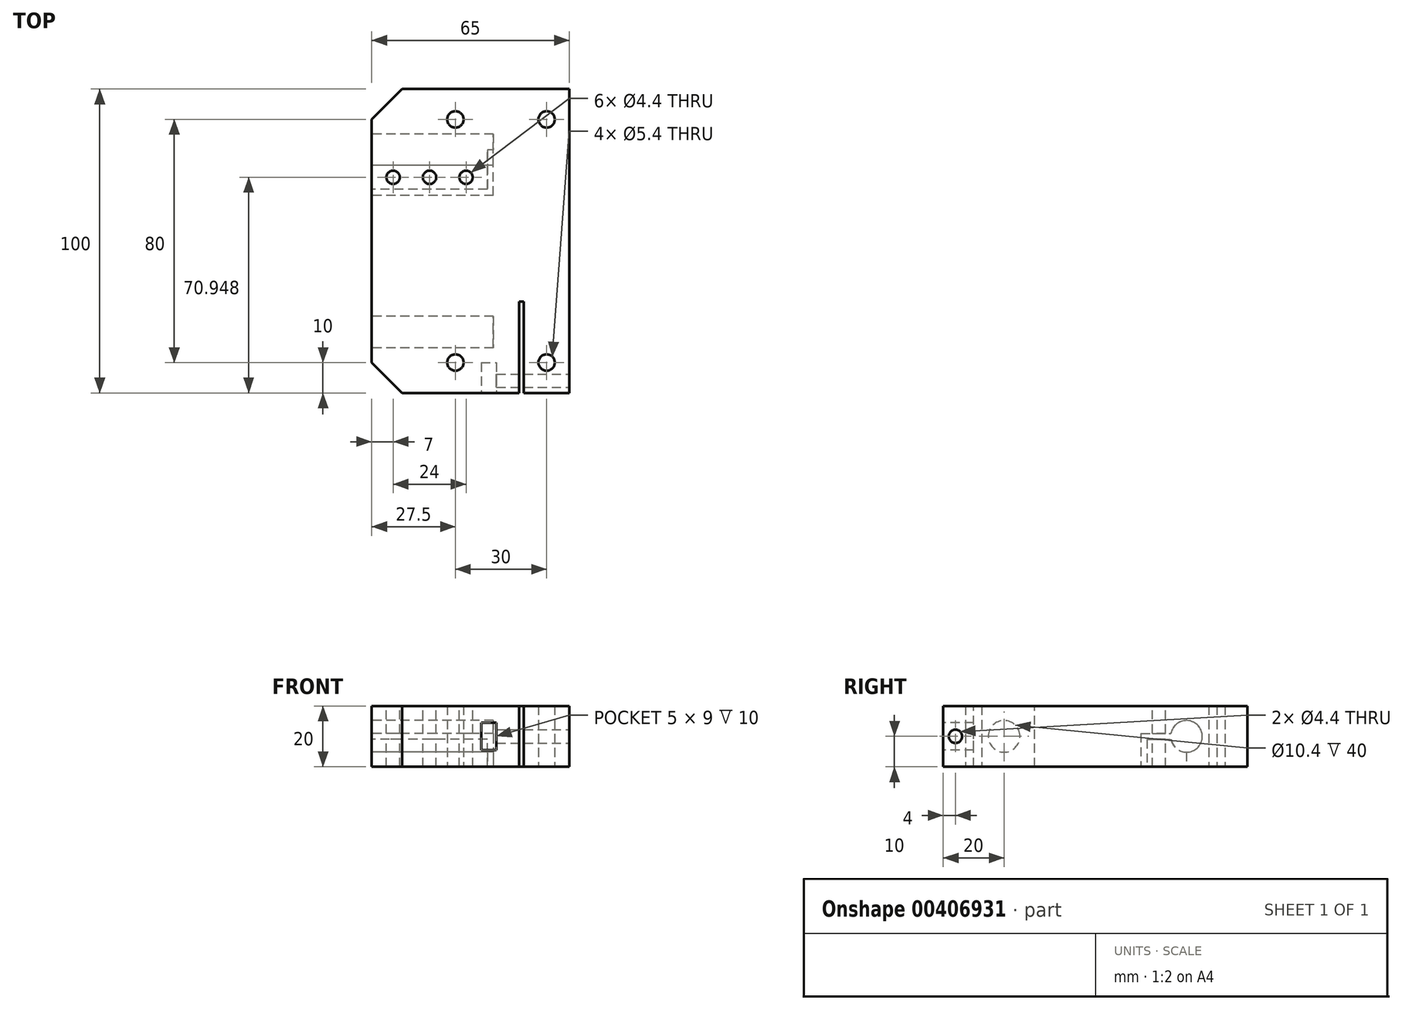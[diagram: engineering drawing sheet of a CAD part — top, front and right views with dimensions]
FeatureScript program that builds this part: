
annotation { "Feature Type Name" : "Feature", "Feature Type Description" : "" }
export const myFeature = defineFeature(function(context is Context, id is Id, definition is map)
    precondition{}
    {
        {
            var Q0;
            Q0=qCreatedBy(makeId("Top.planeOp"),FACE);
            var sketch = newSketch(context, id + "F0", { "sketchPlane" : qUnion([Q0])});
            skLineSegment(sketch, "E0", {"start": v(-15, 15.7) * mm, "end": v(-15, -27.72) * mm, "construction": true});
            skCircle(sketch, "E1", {"center": v(-15, 40) * mm, "radius": 2.7 * mm});
            skCircle(sketch, "E2", {"center": v(-15, -40) * mm, "radius": 2.7 * mm});
            skCircle(sketch, "E3.MirrorC", {"center": v(15, 40) * mm, "radius": 2.7 * mm});
            skCircle(sketch, "E4.MirrorC", {"center": v(15, -40) * mm, "radius": 2.7 * mm});
            skLineSegment(sketch, "E5.bottom", {"start": v(22.5, -50) * mm, "end": v(-22.5, -50) * mm});
            skLineSegment(sketch, "E5.top", {"start": v(22.5, 50) * mm, "end": v(-22.5, 50) * mm});
            skLineSegment(sketch, "E5.left", {"start": v(22.5, -50) * mm, "end": v(22.5, 50) * mm});
            skLineSegment(sketch, "E5.right", {"start": v(-22.5, -50) * mm, "end": v(-22.5, 50) * mm});
            skPoint(sketch, "E5.middle", {"position": v(0, 0) * mm});
            skSolve(sketch);
        }
        {
            var Q0;
            Q0 = qSketchRegion(id + "F0", true);
            extrude(context, id + "F1", {"entities" : qUnion([Q0]), "depth" : 20 * mm});
        }
        {
            var Q0;
            Q0=makeQuery(id+"F1.opExtrude","CAP_FACE",FACE,{"disambiguationData":[OSD([sQuery(id+"F0.wireOp",EDGE,"E1"),sQuery(id+"F0.wireOp",EDGE,"E2"),sQuery(id+"F0.wireOp",EDGE,"E3.MirrorC"),sQuery(id+"F0.wireOp",EDGE,"E4.MirrorC"),sQuery(id+"F0.wireOp",EDGE,"E5.bottom"),sQuery(id+"F0.wireOp",EDGE,"E5.top"),sQuery(id+"F0.wireOp",EDGE,"E5.left"),sQuery(id+"F0.wireOp",EDGE,"E5.right")])],"isStart":false});
            var sketch = newSketch(context, id + "F2", { "sketchPlane" : qUnion([Q0])});
            skLineSegment(sketch, "E6.bottom", {"start": v(7.5, -50) * mm, "end": v(6, -50) * mm});
            skLineSegment(sketch, "E6.top", {"start": v(7.5, -20) * mm, "end": v(6, -20) * mm});
            skLineSegment(sketch, "E6.left", {"start": v(7.5, -50) * mm, "end": v(7.5, -20) * mm});
            skLineSegment(sketch, "E6.right", {"start": v(6, -50) * mm, "end": v(6, -20) * mm});
            skSolve(sketch);
        }
        {
            var Q0;
            Q0 = qSketchRegion(id + "F2", true);
            extrude(context, id + "F3", {"entities" : qUnion([Q0]), "operationType" : NewBodyOperationType.REMOVE, "oppositeDirection" : true, "depth" : 25 * mm});
        }
        {
            var Q0;
            Q0=makeQuery(id+"F1.opExtrude","SWEPT_FACE",FACE,{"disambiguationData":[OSD([sQuery(id+"F0.wireOp",EDGE,"E5.left")])]});
            var sketch = newSketch(context, id + "F4", { "sketchPlane" : qUnion([Q0])});
            skLineSegment(sketch, "E7", {"start": v(-46, 20) * mm, "end": v(-46, 0) * mm, "construction": true});
            skCircle(sketch, "E8", {"center": v(-46, 10) * mm, "radius": 2.2 * mm});
            skSolve(sketch);
        }
        {
            var Q0;
            Q0 = qSketchRegion(id + "F4", true);
            extrude(context, id + "F5", {"entities" : qUnion([Q0]), "operationType" : NewBodyOperationType.REMOVE, "oppositeDirection" : true, "depth" : 25 * mm});
        }
        {
            var Q0;
            Q0=makeQuery(id+"F1.opExtrude","SWEPT_FACE",FACE,{"disambiguationData":[OSD([sQuery(id+"F0.wireOp",EDGE,"E5.right")])]});
            extrude(context, id + "F6", {"entities" : qUnion([Q0]), "operationType" : NewBodyOperationType.ADD, "depth" : 20 * mm});
        }
        {
            var Q0;
            Q0=makeQuery(id+"F6.opExtrude","CAP_FACE",FACE,{"disambiguationData":[OSD([sQuery(id+"F0.wireOp",EDGE,"E5.right")])],"isStart":false});
            var sketch = newSketch(context, id + "F7", { "sketchPlane" : qUnion([Q0])});
            skLineSegment(sketch, "E9", {"start": v(-50, 10) * mm, "end": v(50, 10) * mm, "construction": true});
            skCircle(sketch, "E10", {"center": v(-30, 10) * mm, "radius": 5.2 * mm});
            skCircle(sketch, "E11.MirrorC", {"center": v(30, 10) * mm, "radius": 5.2 * mm});
            skSolve(sketch);
        }
        {
            var Q0;
            Q0 = qSketchRegion(id + "F7", true);
            extrude(context, id + "F8", {"entities" : qUnion([Q0]), "operationType" : NewBodyOperationType.REMOVE, "oppositeDirection" : true, "depth" : 40 * mm});
        }
        {
            var Q0;
            Q0=makeQuery(id+"F6.opExtrude","CAP_FACE",FACE,{"disambiguationData":[OSD([sQuery(id+"F0.wireOp",EDGE,"E5.right")])],"isStart":false});
            var sketch = newSketch(context, id + "F9", { "sketchPlane" : qUnion([Q0])});
            skLineSegment(sketch, "E12", {"start": v(-50, 10) * mm, "end": v(50, 10) * mm, "construction": true});
            skLineSegment(sketch, "E13.bottom", {"start": v(-15, 9) * mm, "end": v(-30, 9) * mm});
            skLineSegment(sketch, "E13.top", {"start": v(-15, 11) * mm, "end": v(-30, 11) * mm});
            skLineSegment(sketch, "E13.left", {"start": v(-15, 9) * mm, "end": v(-15, 11) * mm});
            skLineSegment(sketch, "E13.right", {"start": v(-30, 9) * mm, "end": v(-30, 11) * mm});
            skPoint(sketch, "E13.middle", {"position": v(-22.5, 10) * mm});
            skLineSegment(sketch, "E14.bottom", {"start": v(-15, 9) * mm, "end": v(-17, 9) * mm});
            skLineSegment(sketch, "E14.top", {"start": v(-15, 0) * mm, "end": v(-17, 0) * mm});
            skLineSegment(sketch, "E14.left", {"start": v(-15, 9) * mm, "end": v(-15, 0) * mm});
            skLineSegment(sketch, "E14.right", {"start": v(-17, 9) * mm, "end": v(-17, 0) * mm});
            skSolve(sketch);
        }
        {
            var Q0;
            Q0 = qSketchRegion(id + "F9", true);
            extrude(context, id + "F10", {"entities" : qUnion([Q0]), "operationType" : NewBodyOperationType.REMOVE, "oppositeDirection" : true, "depth" : 40 * mm});
        }
        {
            var Q0;
            {var subQ0=sQuery(id+"F0.wireOp",EDGE,"E5.right");Q0=makeQuery(id+"F6.boolean.opBoolean","MERGE",FACE,{"derivedFrom":[makeQuery(id+"F1.opExtrude","CAP_FACE",FACE,{"disambiguationData":[OSD([sQuery(id+"F0.wireOp",EDGE,"E1"),sQuery(id+"F0.wireOp",EDGE,"E2"),sQuery(id+"F0.wireOp",EDGE,"E3.MirrorC"),sQuery(id+"F0.wireOp",EDGE,"E4.MirrorC"),sQuery(id+"F0.wireOp",EDGE,"E5.bottom"),sQuery(id+"F0.wireOp",EDGE,"E5.top"),sQuery(id+"F0.wireOp",EDGE,"E5.left"),subQ0])],"isStart":true}),makeQuery(id+"F6.opExtrude","SWEPT_FACE",FACE,{"disambiguationData":[OSD([subQ0]),TDD([makeQuery(id+"F1.opExtrude","CAP_EDGE",EDGE,{"disambiguationData":[OSD([subQ0])],"isStart":true})])]})]});}
            var sketch = newSketch(context, id + "F11", { "sketchPlane" : qUnion([Q0])});
            skLineSegment(sketch, "E15.bottom", {"start": v(-2.5, -15) * mm, "end": v(-4.5, -15) * mm});
            skLineSegment(sketch, "E15.top", {"start": v(-2.5, -30) * mm, "end": v(-4.5, -30) * mm});
            skLineSegment(sketch, "E15.left", {"start": v(-2.5, -15) * mm, "end": v(-2.5, -30) * mm});
            skLineSegment(sketch, "E15.right", {"start": v(-4.5, -15) * mm, "end": v(-4.5, -30) * mm});
            skSolve(sketch);
        }
        {
            var Q0;
            Q0 = qSketchRegion(id + "F11", true);
            extrude(context, id + "F12", {"entities" : qUnion([Q0]), "operationType" : NewBodyOperationType.REMOVE, "oppositeDirection" : true, "depth" : 10 * mm});
        }
        {
            var Q0;
            Q0=makeQuery(id+"F10.boolean.opBoolean","COPY",FACE,{"derivedFrom":makeQuery(id+"F10.opExtrude","SWEPT_FACE",FACE,{"disambiguationData":[OSD([sQuery(id+"F9.wireOp",EDGE,"E13.bottom")])]})});
            var sketch = newSketch(context, id + "F13", { "sketchPlane" : qUnion([Q0])});
            skLineSegment(sketch, "E16", {"start": v(-42.5, 20.95) * mm, "end": v(-4.5, 20.95) * mm, "construction": true});
            skCircle(sketch, "E17", {"center": v(-35.5, 20.95) * mm, "radius": 2.2 * mm});
            skCircle(sketch, "E18", {"center": v(-11.5, 20.95) * mm, "radius": 2.2 * mm});
            skCircle(sketch, "E19", {"center": v(-23.5, 20.95) * mm, "radius": 2.2 * mm});
            skSolve(sketch);
        }
        {
            var Q0;
            Q0 = qSketchRegion(id + "F13", true);
            extrude(context, id + "F14", {"entities" : qUnion([Q0]), "operationType" : NewBodyOperationType.REMOVE, "endBound" : BoundingType.SYMMETRIC, "oppositeDirection" : true, "depth" : 50 * mm});
        }
        {
            var Q0;
            Q0=makeQuery(id+"F6.opExtrude","CAP_EDGE",EDGE,{"disambiguationData":[OSD([sQuery(id+"F0.wireOp",EDGE,"E5.top"),sQuery(id+"F0.wireOp",EDGE,"E5.right")])],"isStart":false});
            var Q1;
            Q1=makeQuery(id+"F6.opExtrude","CAP_EDGE",EDGE,{"disambiguationData":[OSD([sQuery(id+"F0.wireOp",EDGE,"E5.bottom"),sQuery(id+"F0.wireOp",EDGE,"E5.right")])],"isStart":false});
            chamfer(context, id + "F15", {"entities" : qUnion([Q0, Q1]), "width" : 10 * mm, "tangentPropagation" : true});
        }
        {
            var Q0;
            {var subQ0=sQuery(id+"F0.wireOp",EDGE,"E5.right");var subQ1=sQuery(id+"F0.wireOp",EDGE,"E5.bottom");Q0=makeQuery(id+"F6.boolean.opBoolean","MERGE",FACE,{"derivedFrom":[makeQuery(id+"F3.boolean.opBoolean","SPLIT",FACE,{"disambiguationData":[TD([makeQuery(id+"F1.opExtrude","SWEPT_FACE",FACE,{"disambiguationData":[OSD([subQ0])]})])],"derivedFrom":makeQuery(id+"F1.opExtrude","SWEPT_FACE",FACE,{"disambiguationData":[OSD([subQ1])]})}),makeQuery(id+"F6.opExtrude","SWEPT_FACE",FACE,{"disambiguationData":[OSD([subQ1,subQ0])]})]});}
            var sketch = newSketch(context, id + "F16", { "sketchPlane" : qUnion([Q0])});
            skLineSegment(sketch, "E20", {"start": v(6, 10) * mm, "end": v(-14.9, 10) * mm, "construction": true});
            skLineSegment(sketch, "E21.bottom", {"start": v(-6.5, 5.5) * mm, "end": v(-1.5, 5.5) * mm});
            skLineSegment(sketch, "E21.top", {"start": v(-6.5, 14.5) * mm, "end": v(-1.5, 14.5) * mm});
            skLineSegment(sketch, "E21.left", {"start": v(-6.5, 5.5) * mm, "end": v(-6.5, 14.5) * mm});
            skLineSegment(sketch, "E21.right", {"start": v(-1.5, 5.5) * mm, "end": v(-1.5, 14.5) * mm});
            skPoint(sketch, "E21.middle", {"position": v(-4, 10) * mm});
            skSolve(sketch);
        }
        {
            var Q0;
            Q0 = qSketchRegion(id + "F16", true);
            extrude(context, id + "F17", {"entities" : qUnion([Q0]), "operationType" : NewBodyOperationType.REMOVE, "oppositeDirection" : true, "depth" : 10 * mm});
        }
    });
